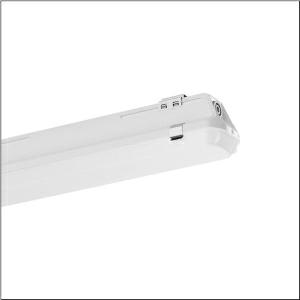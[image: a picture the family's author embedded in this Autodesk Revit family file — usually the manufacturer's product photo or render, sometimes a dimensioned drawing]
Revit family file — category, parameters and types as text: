
# Revit family: monsun_r__21_51fb10mp680b_ab58
name_source: partatom
category: Lighting Fixtures
units: mm (PartAtom-declared; Revit-internal decimal feet)

## family parameters
Cut with Voids When Loaded = No
Host = Face
Light Source = No
Part Type = Normal
Room Calculation Point = No
Round Connector Dimension = Use Diameter
Shared = No

## types (1)
- --- (1 x LED, 8190 lm, 53.6 W, 6500K)
    Apparent Load = 54 VA
    CIE Flux Codes = 47 77 93 94 100
    Color Rendering = 80
    Color Temperature = 6500K
    Default Elevation = 1800 mm
    Description = Monsun® 21, damp-proof luminaire, chain hanger, primary optical cover: enclosure, of PMMA, light emission: direct distribution, primary light characteristic: symmetric, installation type: suspended mounting, surface-mounted, horizontal mounting, vertical mounting, LED, rated luminous flux: 8.190lm, luminous efficacy: 153lm/W, light colour: 865, colour temperature: 6500K, control gear: ECG, with terminal, 3-pole, max. 2.5mm², mains connection: 220..240V, AC, 50/60Hz, rated input power: 54W, housing, of glass-fibre reinforced polyester, uncoated, bright grey, incl. chain hanger, length: 1.590mm, width: 90mm, height: 88mm, clip for enclosure, of stainless steel (V2A), ceiling mounting element, of stainless steel (V2A), chain hanger, of stainless steel (V2A), protection rating (complete): IP66, insulation class (complete): insulation class I (protective earthing), certification: CE, ENEC, VDE, UKCA, protection symbol: D, impact resistance: IK04, permissible operating ambient temperature: -25..+35°C, standard: EN 50419, EN 60598-2-1, corresponds to IFS (International Featured Standards) requirements for safety and quality in the food industry, for indoor or canopied outdoor use, no direct snow, no direct sun, no direct rain, contact your sales advisor before using the luminaires in applications with unclear chemical exposure, large temperature fluctuations or condensation-forming humidity, LABS conformity tested according to VDMA 24364:2018-05, packaging unit: 1 piece
    Height = 89 mm
    Lamp = 1 x LED
    Lamp Light Flux = 8190 lm
    Lamp Power = 53.6 W
    Lamp count = 1
    Length = 1590 mm
    Luminous efficacy = 153 lm/W
    Manufacturer = Siteco
    ModVariant = No
    Model = 51FB10MP680B
    Mounting Place = Ceiling
    Mounting Type = Surface mounted
    Number of Poles = 1
    OnlyDefault = Yes
    Power Factor = 1
    Product Name = Monsun® 21
    Product group = damp-proof luminaire
    ProductGroupID = 301
    Protection Class = Protection class I
    Protection Degree = IP 66
    RLX_Detail_Level = 1
    RLX_Emergency_Light_Flux = 0 lm
    RLX_Emergency_Type = 0
    RLX_Emergency_Type_DB = No
    RlxData = <blob elided: 89901 chars, md5=a884310f>
    Socket = socket
    Standby Power = 0 W
    System Light Flux = 8190 lm
    System Power = 54 W
    Type Comments = factory setting: luminous flux: 100 % | (A | C | E) | 121 mA
    Type Image = l_1006717.jpg
    URL = http://relux.com
    VarID = @adj_096967
    Voltage = 0 V
    Weight = 0.00 kg
    Width = 90 mm

## geometry (parser evidence)
native form markers: Blend x4, Sweep x14
no freeform markers — native parametric forms only
